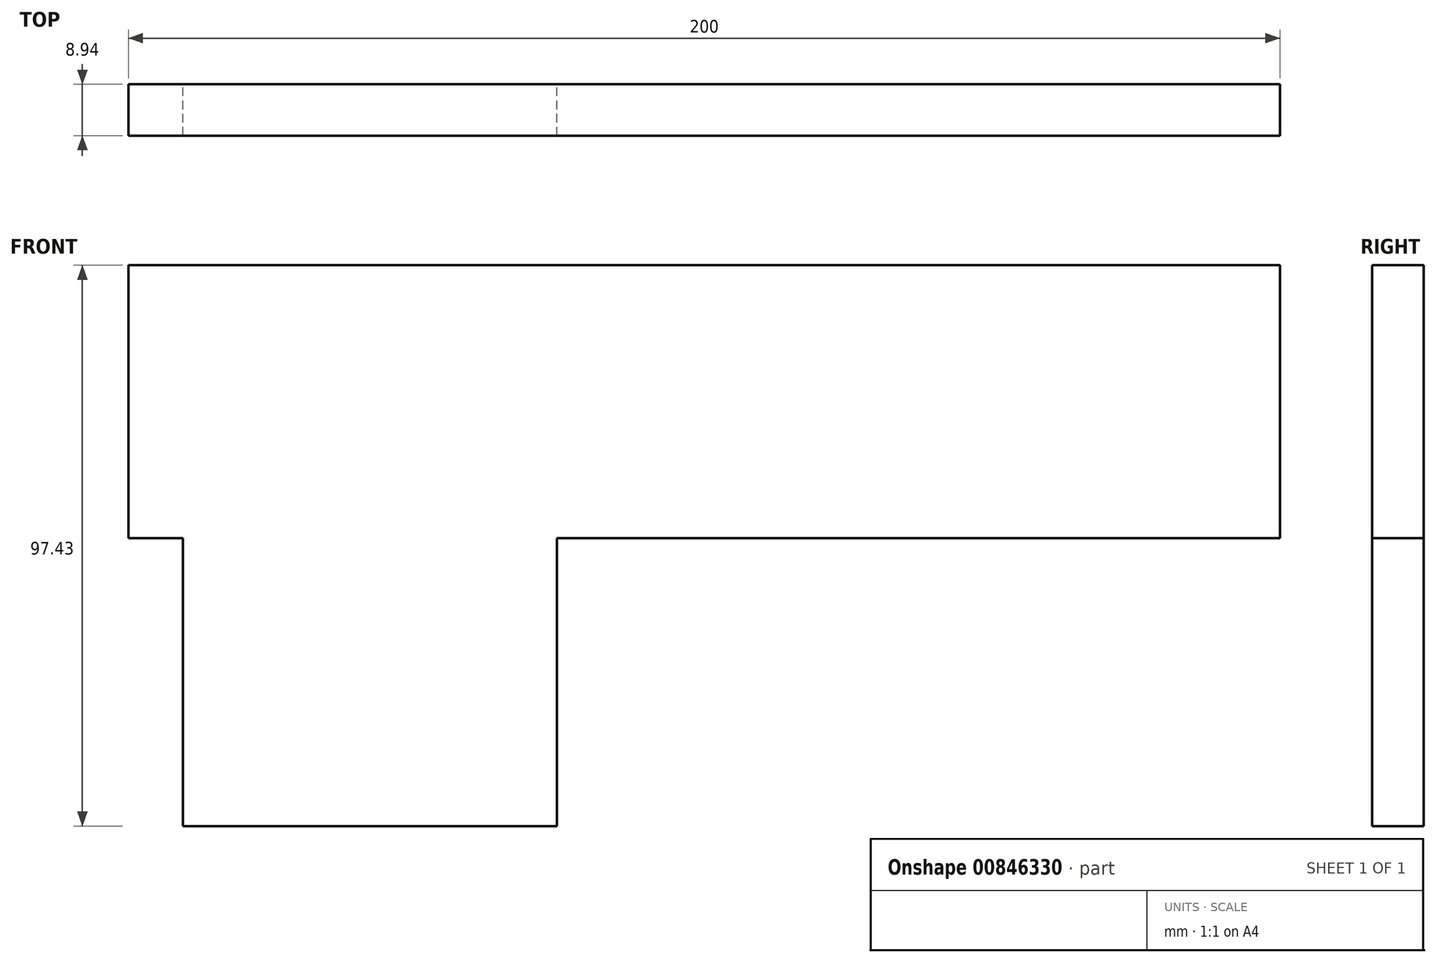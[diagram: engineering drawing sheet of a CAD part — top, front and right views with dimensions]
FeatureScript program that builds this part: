
annotation { "Feature Type Name" : "Feature", "Feature Type Description" : "" }
export const myFeature = defineFeature(function(context is Context, id is Id, definition is map)
    precondition{}
    {
        {
            var Q0;
            Q0=qCreatedBy(makeId("Right.planeOp"),FACE);
            var sketch = newSketch(context, id + "F0", { "sketchPlane" : qUnion([Q0])});
            skLineSegment(sketch, "E0", {"start": v(0, 53.13) * mm, "end": v(0, 38.6) * mm});
            skLineSegment(sketch, "E1", {"start": v(0, 38.6) * mm, "end": v(-11.97, 32.33) * mm});
            skLineSegment(sketch, "E2", {"start": v(-11.97, 32.33) * mm, "end": v(-11.97, -20.25) * mm});
            skLineSegment(sketch, "E3", {"start": v(-11.97, -20.25) * mm, "end": v(0, -27.85) * mm});
            skLineSegment(sketch, "E4", {"start": v(0, -27.85) * mm, "end": v(0, -41.72) * mm});
            skLineSegment(sketch, "E5", {"start": v(0, -41.72) * mm, "end": v(5.48, -41.72) * mm});
            skLineSegment(sketch, "E6", {"start": v(5.48, -41.72) * mm, "end": v(5.48, -27.85) * mm});
            skLineSegment(sketch, "E7", {"start": v(5.48, -27.85) * mm, "end": v(-6.49, -20.25) * mm});
            skLineSegment(sketch, "E8", {"start": v(-6.49, -20.25) * mm, "end": v(-6.49, 32.33) * mm});
            skLineSegment(sketch, "E9", {"start": v(-6.49, 32.33) * mm, "end": v(5.48, 38.6) * mm});
            skLineSegment(sketch, "E10", {"start": v(5.48, 38.6) * mm, "end": v(5.48, 53.13) * mm});
            skLineSegment(sketch, "E11", {"start": v(5.48, 53.13) * mm, "end": v(0, 53.13) * mm});
            skSolve(sketch);
        }
        {
            var Q0;
            Q0 = qConstructionFilter(qBodyType(qCreatedBy(id + "F0" ,EDGE), BodyType.WIRE), ConstructionObject.NO);
            extrude(context, id + "F1", {"bodyType" : ToolBodyType.SURFACE, "surfaceEntities" : qUnion([Q0]), "depth" : 60 * mm, "offsetDistance" : 25 * mm});
        }
        {
            var Q0;
            Q0=makeQuery(id+"F1.opExtrude","SWEPT_EDGE",EDGE,{"disambiguationData":[OSD([sQuery(id+"F0.wireOp",VERTEX,"E2.start")])]});
            fillet(context, id + "F2", {"entities" : qUnion([Q0]), "radius" : 5 * mm, "tangentPropagation" : true, "allowEdgeOverflow" : false});
        }
        {
            var Q0;
            Q0=makeQuery(id+"F1.opExtrude","SWEPT_EDGE",EDGE,{"disambiguationData":[OSD([sQuery(id+"F0.wireOp",VERTEX,"E1.start")])]});
            fillet(context, id + "F3", {"entities" : qUnion([Q0]), "radius" : 5 * mm, "tangentPropagation" : true, "allowEdgeOverflow" : false});
        }
        {
            var Q0;
            Q0=makeQuery(id+"F1.opExtrude","SWEPT_EDGE",EDGE,{"disambiguationData":[OSD([sQuery(id+"F0.wireOp",VERTEX,"E9.start")])]});
            fillet(context, id + "F4", {"entities" : qUnion([Q0]), "radius" : 5 * mm, "tangentPropagation" : true, "allowEdgeOverflow" : false});
        }
        {
            var Q0;
            Q0=makeQuery(id+"F1.opExtrude","SWEPT_EDGE",EDGE,{"disambiguationData":[OSD([sQuery(id+"F0.wireOp",VERTEX,"E8.start")])]});
            fillet(context, id + "F5", {"entities" : qUnion([Q0]), "radius" : 5 * mm, "tangentPropagation" : true, "allowEdgeOverflow" : false});
        }
        {
            var Q0;
            Q0=makeQuery(id+"F1.opExtrude","SWEPT_EDGE",EDGE,{"disambiguationData":[OSD([sQuery(id+"F0.wireOp",VERTEX,"E7.start")])]});
            fillet(context, id + "F6", {"entities" : qUnion([Q0]), "radius" : 5 * mm, "tangentPropagation" : true, "allowEdgeOverflow" : false});
        }
        {
            var Q0;
            Q0=makeQuery(id+"F1.opExtrude","SWEPT_EDGE",EDGE,{"disambiguationData":[OSD([sQuery(id+"F0.wireOp",VERTEX,"E3.start")])]});
            fillet(context, id + "F7", {"entities" : qUnion([Q0]), "radius" : 5 * mm, "tangentPropagation" : true, "allowEdgeOverflow" : false});
        }
        {
            var Q0;
            Q0=makeQuery(id+"F1.opExtrude","SWEPT_EDGE",EDGE,{"disambiguationData":[OSD([sQuery(id+"F0.wireOp",VERTEX,"E4.start")])]});
            fillet(context, id + "F8", {"entities" : qUnion([Q0]), "radius" : 5 * mm, "tangentPropagation" : true, "allowEdgeOverflow" : false});
        }
        {
            var Q0;
            Q0=qCreatedBy(makeId("Right.planeOp"),FACE);
            var sketch = newSketch(context, id + "F9", { "sketchPlane" : qUnion([Q0])});
            skLineSegment(sketch, "E12", {"start": v(-3.24, 31.2) * mm, "end": v(-3.24, -16.22) * mm});
            skLineSegment(sketch, "E13", {"start": v(-3.24, -16.22) * mm, "end": v(5.7, -16.22) * mm});
            skLineSegment(sketch, "E14", {"start": v(5.7, -16.22) * mm, "end": v(5.7, 31.2) * mm});
            skLineSegment(sketch, "E15", {"start": v(5.7, 31.2) * mm, "end": v(-3.24, 31.2) * mm});
            skSolve(sketch);
        }
        {
            var Q0;
            Q0 = qSketchRegion(id + "F9", true);
            extrude(context, id + "F10", {"entities" : qUnion([Q0]), "endBound" : BoundingType.SYMMETRIC, "oppositeDirection" : true, "depth" : 200 * mm, "offsetDistance" : 25 * mm});
        }
        {
            var Q0;
            Q0=makeQuery(id+"F10.opExtrude","SWEPT_FACE",FACE,{"disambiguationData":[OSD([sQuery(id+"F9.wireOp",EDGE,"E13")])]});
            var sketch = newSketch(context, id + "F11", { "sketchPlane" : qUnion([Q0])});
            skLineSegment(sketch, "E16.bottom", {"start": v(-90.56, 3.24) * mm, "end": v(-25.56, 3.24) * mm});
            skLineSegment(sketch, "E16.top", {"start": v(-90.56, -5.7) * mm, "end": v(-25.56, -5.7) * mm});
            skLineSegment(sketch, "E16.left", {"start": v(-90.56, 3.24) * mm, "end": v(-90.56, -5.7) * mm});
            skLineSegment(sketch, "E16.right", {"start": v(-25.56, 3.24) * mm, "end": v(-25.56, -5.7) * mm});
            skSolve(sketch);
        }
        {
            var Q0;
            Q0 = qSketchRegion(id + "F11", true);
            extrude(context, id + "F12", {"entities" : qUnion([Q0]), "operationType" : NewBodyOperationType.ADD, "depth" : 50 * mm, "offsetDistance" : 25 * mm});
        }
    });
